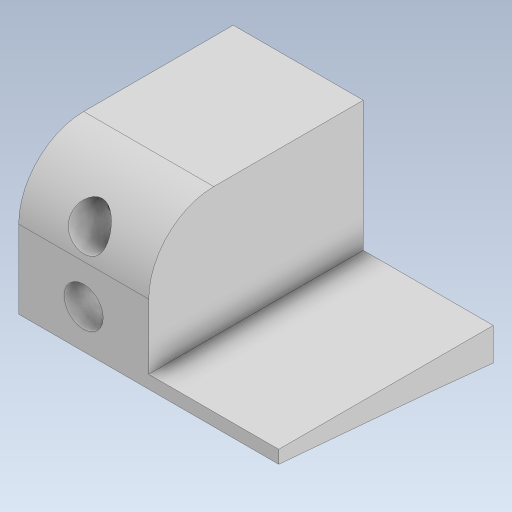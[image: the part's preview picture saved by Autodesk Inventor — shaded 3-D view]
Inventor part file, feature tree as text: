
AUTODESK INVENTOR PART (.ipt)
format: ipt  version: 2023.5 (Build 275446000, 446)  size: 206,848 bytes
history: native  units: in
note: dims shown in document units (in); Inventor stores cm internally (conversion verified against a paired STEP export)
features: extrude x10, sketch x8, plane x3, fillet x1
ambient origin geometry x8: Origin, YZ Plane, XZ Plane, XY Plane, X Axis, Y Axis, Z Axis, Center Point
bodies: Solid1 (feature_tree)
feature tree (22):
  sketch  "Sketch1"  dims[d0=0.7874in d1=0.5118in]
  extrude  "Extrusion1"  Depth=0.5118in
  extrude  "Extrusion2"  Depth=0.1181in
  extrude  "Extrusion3"  Depth=0.3937in TaperAngle=0.0deg
  plane  "Work Plane1"
  extrude  "Extrusion4"  Depth=0.0787in TaperAngle=0.0deg
  fillet  "Fillet1"  Radius=0.7874in
  extrude  "Extrusion5"  Depth=0.1181in
  plane  "Work Plane2"
  extrude  "Extrusion6"  Depth=0.1181in
  extrude  "Extrusion7"  Depth=0.7874in TaperAngle=0.0deg
  plane  "Work Plane3"
  extrude  "Extrusion8"  Depth=0.3937in
  extrude  "Extrusion9"  Depth=0.3937in TaperAngle=0.0deg
  extrude  "Extrusion10"  Depth=0.3937in TaperAngle=0.0deg
  sketch  "Sketch2"  dims[d2=0.7874in d3=0.1181in]
  sketch  "Sketch3"  dims[d4=0.3937in d5=0.0787in d6=0.0in]
  sketch  "Sketch4"  dims[d7=0.8661in d8=0.0in d9=0.0787in d10=0.0in d11=0.7874in d12=0.0in]
  sketch  "Sketch5"  dims[d13=0.3937in d14=0.1181in]
  sketch  "Sketch6"  dims[d15=0.2362in d16=0.1181in]
  sketch  "Sketch7"  dims[d18=0.2362in d19=0.7874in d20=0.0in]
  sketch  "Sketch8"  dims[d21=0.2362in d22=0.2362in d23=0.7874in d24=0.0in d25=0.3937in d26=0.0in d27=0.0787in d28=1.5748in d29=0.0in d30=0.3937in d31=0.0in d32=0.0394in d33=1.5748in d34=0.0in]
